# Revit family: NBS_DudleyIndustries_WshTrghs_WuduWashStation
name_source: partatom
category: Generic Models
revit_build: Autodesk Revit 2016 (Build: 20150220_1215(x64)
units: mm (PartAtom-declared; Revit-internal decimal feet)

## family parameters
Always vertical = Yes
Can host rebar = No
Cut with Voids When Loaded = No
OmniClass Number = 23.45.30.00
OmniClass Title = Washing and Waste Disposal Equipment
Part Type = Normal
Room Calculation Point = No
Round Connector Dimension = Use Diameter
Shared = No
Work Plane-Based = No

## types (1)
- WuduWashStation
    AssetType = Fixed
    BIMObjectName = NBS_DudleyIndustries_WashTroughs_WuduWashStation
    Category = Pr_40_70_62_37:Hand driers
    Color = Stainless steel, black or white powder coated
    Description = Trough
    DrainSize = 0 mm  [stored 0 ft]
    DurationUnit = year
    EnvironmentalProductDeclaration = Water saving tap
    ExpectedLife = 5
    Features = Uses 90% less water, lower sides to provide clearance to enable easy arm movement, soap tray centrally located to avoid interference when washing arms, hinged foot grate for easy cleaning access, including sump and removable grate to improcmsve cleaning and reduce the risk of blockages, reaches an ambient temperature quickly, auto shut off water isolation valve
    Finish = Brushed
    Grade = 304 Stainless steel
    IfcExportAs = IfcSanitaryTerminalType
    IfcExportType = USERDEFINED
    IntegralAccessories = Soap tray, Lift up hinged grid
    ManufacturerName = Dudley Industries
    ManufacturerURL = www.dudleyindustries.com/
    Material = 304 Stainless steel
    MaterialsBody = 304 Stainless Steel
    MaterialsFinishColour = 204G Brushed
    ModelNumber = 95000
    ModelReference = Wudu Wash Station
    NBSCertification = www.nationalbimlibrary.com/cert/y02lzapm
    NBSDescription = Wash troughs
    NBSReference = 45-35-70/370
    Name = WashTroughs_WuduWashStation_DudleyIndustries
    NominalDepth = 450 mm  [stored 1.47638 ft]
    NominalHeight = 760 mm  [stored 2.49344 ft]
    NominalLength = 450 mm  [stored 1.47638 ft]
    NominalWidth = 510 mm  [stored 1.67323 ft]
    ProductInformation = www.dudleyindustries.com/wp-content/uploads/2017/08/Wudu_Wash_Station_Datasheet.pdf
    SinkMounting = Floor Mounted & Back to Wall
    SinkType = Trough
    Size = 510 x 760 x 450 mm
    Stations = One
    TapLength = 167 mm
    TroughMaterial = NBS_Concept
    TroughTapMaterial = NBS_Concept
    Uniclass2015Code = Pr_40_20_96_99
    Uniclass2015Title = Wash troughs
    Uniclass2015Version = Products v1.7
    Version = 2
    WarrantyDescription = 1 year warranty
    WarrantyDurationParts = 1
    WarrantyDurationUnit = year
    WaterSupplyOverflowAndWasteHolesWaste = Central Outlet
    WaterSupplyOverflowAndWasteHolesWaterSupply = One tap in back positioned centrally

note: [stored X ft] marks values corroborated as IEEE doubles in the binary element streams (Revit-internal decimal feet)

## geometry (parser evidence)
native form markers: Sweep x2
no freeform markers — native parametric forms only
